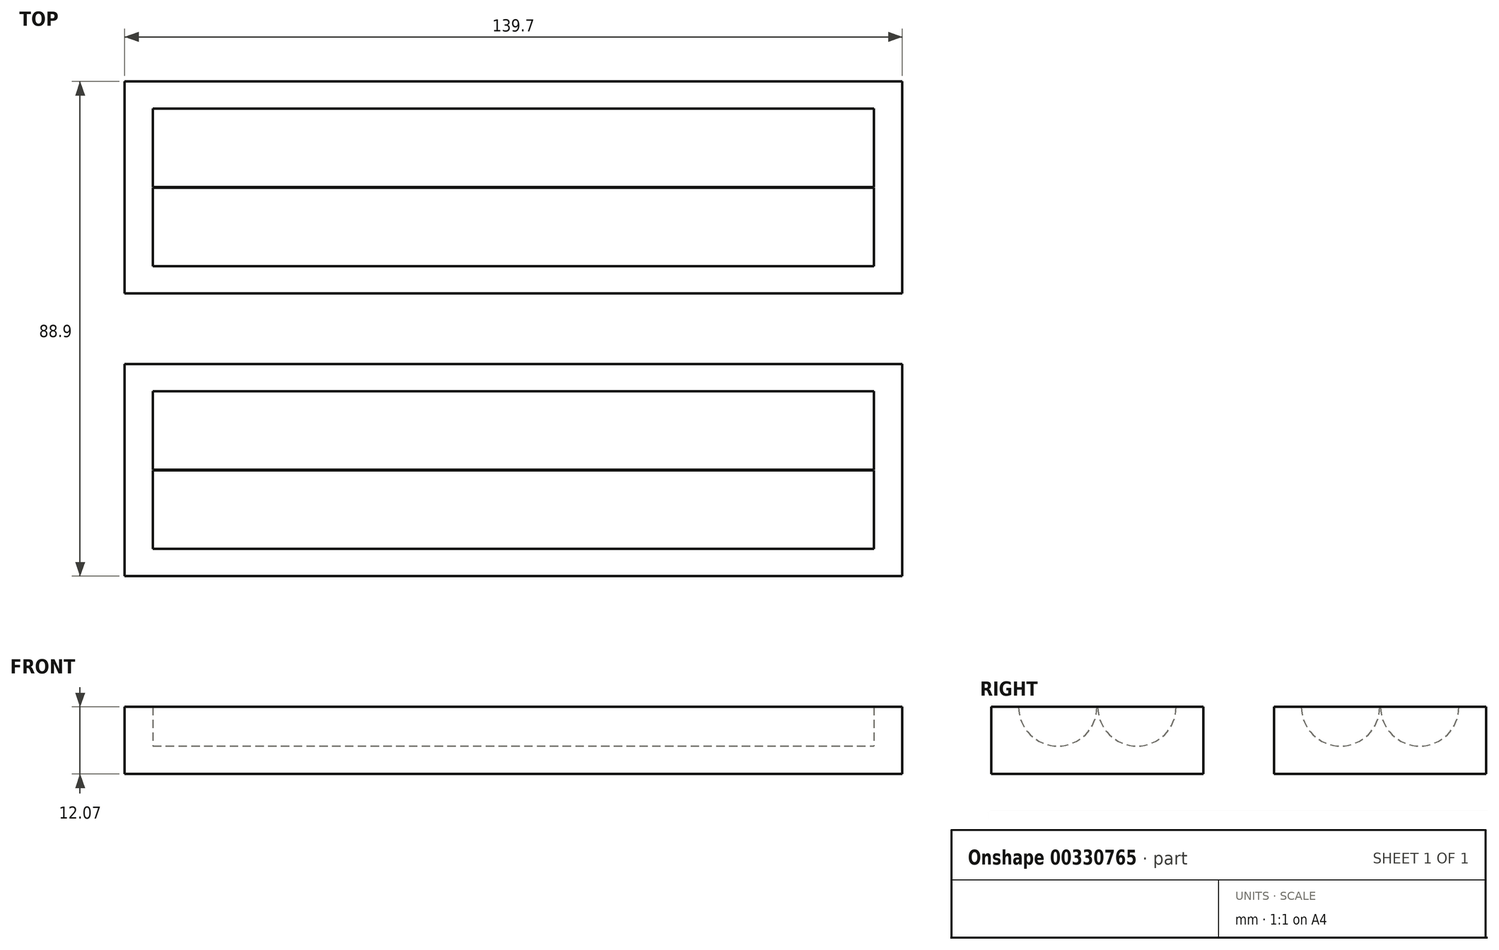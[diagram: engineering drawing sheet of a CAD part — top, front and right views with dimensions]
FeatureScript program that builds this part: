
annotation { "Feature Type Name" : "Feature", "Feature Type Description" : "" }
export const myFeature = defineFeature(function(context is Context, id is Id, definition is map)
    precondition{}
    {
        {
            var Q0;
            Q0=qCreatedBy(makeId("Top.planeOp"),FACE);
            var sketch = newSketch(context, id + "F0", { "sketchPlane" : qUnion([Q0])});
            skLineSegment(sketch, "E0.bottom", {"start": v(69.85, 19.05) * mm, "end": v(-69.85, 19.05) * mm});
            skLineSegment(sketch, "E0.top", {"start": v(69.85, -19.05) * mm, "end": v(-69.85, -19.05) * mm});
            skLineSegment(sketch, "E0.left", {"start": v(69.85, 19.05) * mm, "end": v(69.85, -19.05) * mm});
            skLineSegment(sketch, "E0.right", {"start": v(-69.85, 19.05) * mm, "end": v(-69.85, -19.05) * mm});
            skPoint(sketch, "E0.middle", {"position": v(0, 0) * mm});
            skSolve(sketch);
        }
        {
            var Q0;
            Q0=makeQuery(id+"F0.imprint","IMPRINT",FACE,{"disambiguationData":[TD([[makeQuery(id+"F0.imprint","IMPRINT",EDGE,{"derivedFrom":sQuery(id+"F0.wireOp",EDGE,"E0.bottom")}),1.0]])]});
            extrude(context, id + "F1", {"entities" : qUnion([Q0]), "depth" : 12.06 * mm});
        }
        {
            var Q0;
            Q0=makeQuery(id+"F1.opExtrude","SWEPT_FACE",FACE,{"disambiguationData":[OSD([sQuery(id+"F0.wireOp",EDGE,"E0.left")])]});
            var sketch = newSketch(context, id + "F2", { "sketchPlane" : qUnion([Q0])});
            skCircle(sketch, "E1", {"center": v(-7.11, 12.07) * mm, "radius": 7.04 * mm});
            skCircle(sketch, "E2", {"center": v(7.11, 12.07) * mm, "radius": 7.04 * mm});
            skSolve(sketch);
        }
        {
            var Q0;
            Q0 = qSketchRegion(id + "F2", true);
            extrude(context, id + "F3", {"entities" : qUnion([Q0]), "operationType" : NewBodyOperationType.REMOVE, "oppositeDirection" : true, "depth" : 134.62 * mm, "hasSecondDirection" : true, "secondDirectionOppositeDirection" : true, "secondDirectionDepth" : 5.08 * mm});
        }
        {
            var Q0;
            Q0=makeQuery(id+"F1.opExtrude","SWEPT_BODY",BODY,{"disambiguationData":[OSD([sQuery(id+"F0.wireOp",EDGE,"E0.bottom"),sQuery(id+"F0.wireOp",EDGE,"E0.top"),sQuery(id+"F0.wireOp",EDGE,"E0.left"),sQuery(id+"F0.wireOp",EDGE,"E0.right")])]});
            var Q1;
            Q1=qCreatedBy(makeId("Front.planeOp"),FACE);
            transform(context, id + "F4", {"entities" : qUnion([Q0]), "transformType" : TransformType.TRANSLATION_DISTANCE, "transformDirection" : qUnion([Q1]), "distance" : 50.8 * mm, "oppositeDirection" : true, "makeCopy" : true});
        }
    });
